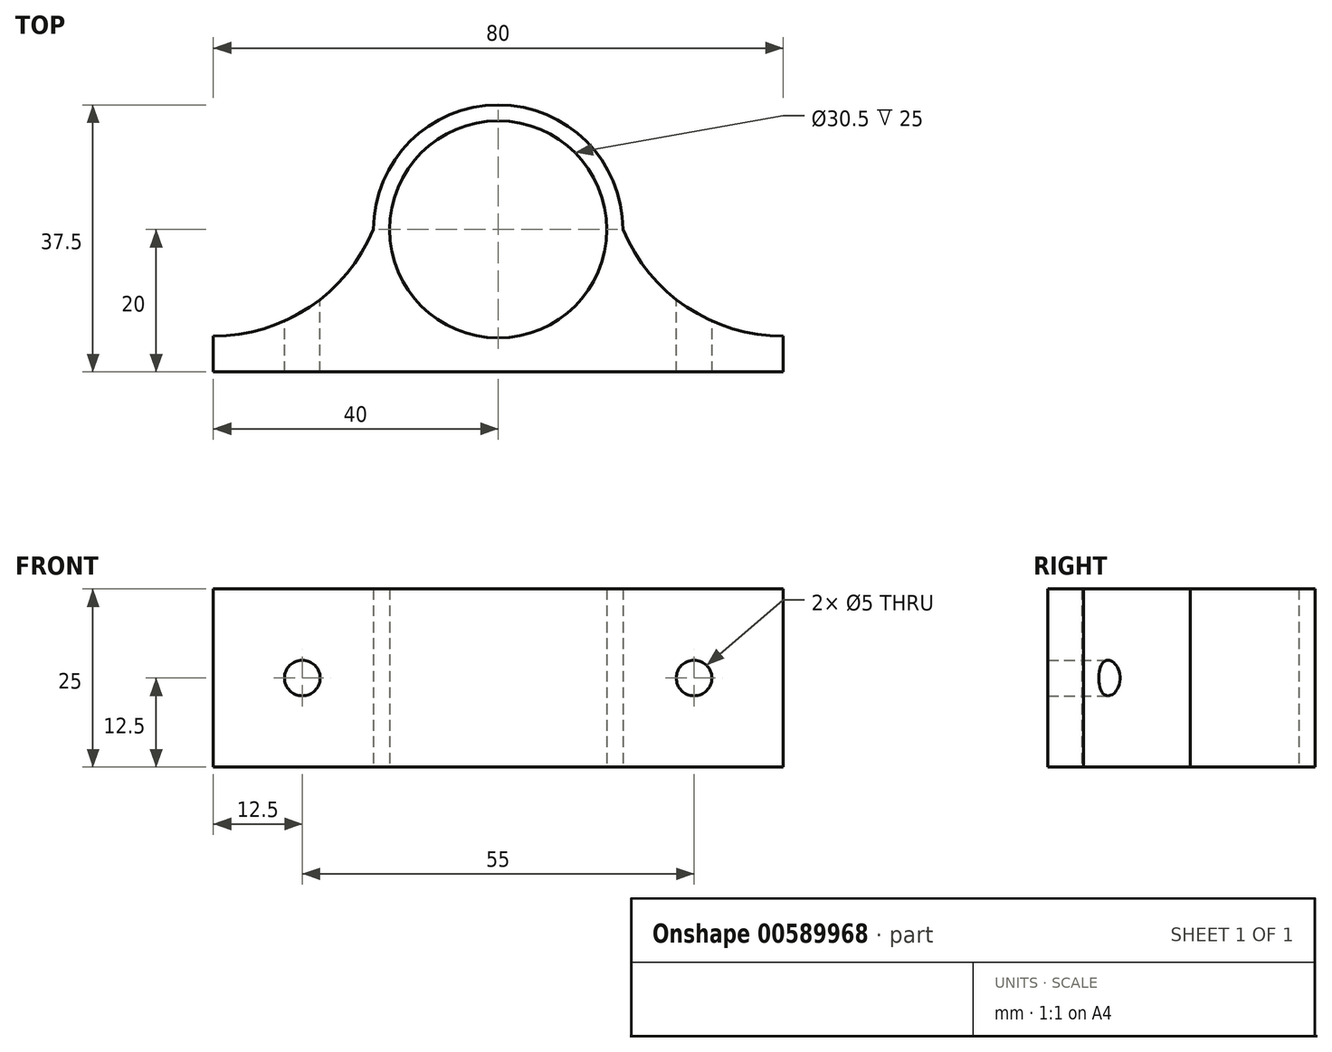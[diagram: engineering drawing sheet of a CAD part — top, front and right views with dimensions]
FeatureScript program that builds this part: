
annotation { "Feature Type Name" : "Feature", "Feature Type Description" : "" }
export const myFeature = defineFeature(function(context is Context, id is Id, definition is map)
    precondition{}
    {
        {
            var Q0;
            Q0=qCreatedBy(makeId("Top.planeOp"),FACE);
            var sketch = newSketch(context, id + "F0", { "sketchPlane" : qUnion([Q0])});
            skArc(sketch, "E0", {"start": v(17.5, 0) * mm, "mid": v(0, 17.5) * mm, "end": v(-17.5, 0) * mm});
            skLineSegment(sketch, "E1.bottom", {"start": v(40, -20) * mm, "end": v(-40, -20) * mm});
            skLineSegment(sketch, "E1.left", {"start": v(40, -20) * mm, "end": v(40, -15) * mm});
            skLineSegment(sketch, "E1.right", {"start": v(-40, -20) * mm, "end": v(-40, -15) * mm});
            skPoint(sketch, "E1.middle", {"position": v(0, -17.5) * mm});
            skArc(sketch, "E2", {"start": v(17.5, 0) * mm, "mid": v(26.48, -10.9) * mm, "end": v(40, -15) * mm});
            skArc(sketch, "E3", {"start": v(-40, -15) * mm, "mid": v(-26.48, -10.9) * mm, "end": v(-17.5, 0) * mm});
            skCircle(sketch, "E4", {"center": v(0, 0) * mm, "radius": 15.25 * mm});
            skSolve(sketch);
        }
        {
            var Q0;
            Q0=makeQuery(id+"F0.imprint","IMPRINT",FACE,{"disambiguationData":[TD([[makeQuery(id+"F0.imprint","IMPRINT",EDGE,{"derivedFrom":sQuery(id+"F0.wireOp",EDGE,"E0")}),1.0]])]});
            extrude(context, id + "F1", {"entities" : qUnion([Q0]), "depth" : 25 * mm, "offsetDistance" : 25 * mm});
        }
        {
            var Q0;
            Q0=qCreatedBy(makeId("Front.planeOp"),FACE);
            var sketch = newSketch(context, id + "F2", { "sketchPlane" : qUnion([Q0])});
            skCircle(sketch, "E5", {"center": v(27.5, 12.5) * mm, "radius": 2.5 * mm});
            skCircle(sketch, "E6", {"center": v(-27.5, 12.5) * mm, "radius": 2.5 * mm});
            skSolve(sketch);
        }
        {
            var Q0;
            Q0 = qSketchRegion(id + "F2", true);
            extrude(context, id + "F3", {"entities" : qUnion([Q0]), "operationType" : NewBodyOperationType.REMOVE, "depth" : 25 * mm, "offsetDistance" : 25 * mm});
        }
    });
